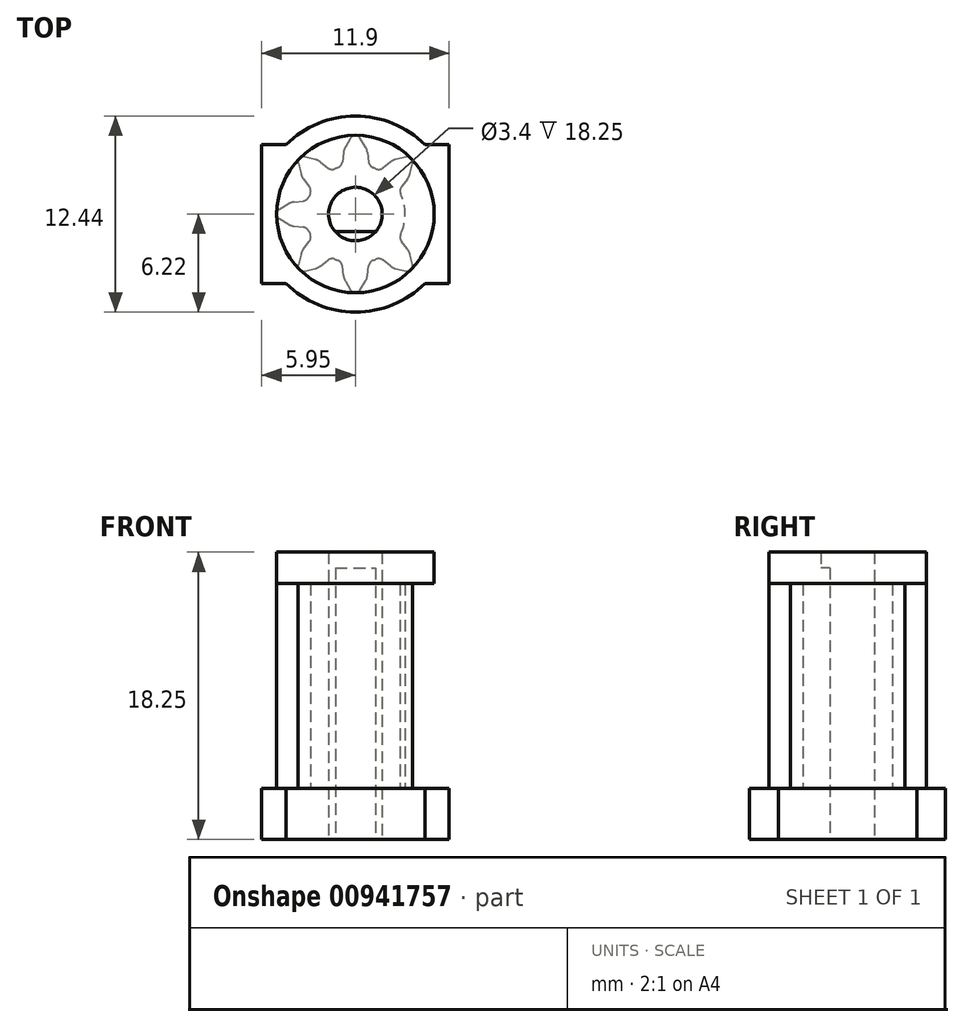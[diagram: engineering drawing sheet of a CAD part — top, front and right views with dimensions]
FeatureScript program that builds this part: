
annotation { "Feature Type Name" : "Feature", "Feature Type Description" : "" }
export const myFeature = defineFeature(function(context is Context, id is Id, definition is map)
    precondition{}
    {
        {
            var Q0;
            Q0=qCreatedBy(makeId("Top.planeOp"),FACE);
            var sketch = newSketch(context, id + "F0", { "sketchPlane" : qUnion([Q0])});
            skCircle(sketch, "E0", {"center": v(0, 0) * mm, "radius": 1.7 * mm});
            skCircle(sketch, "E1", {"center": v(0, 0) * mm, "radius": 2.55 * mm});
            skArc(sketch, "E2", {"start": v(-4.4, -4.4) * mm, "mid": v(0, -6.22) * mm, "end": v(4.4, -4.4) * mm});
            skCircle(sketch, "E3", {"center": v(0, 0) * mm, "radius": 3.15 * mm});
            skCircle(sketch, "E4", {"center": v(0, 0) * mm, "radius": 5 * mm});
            skLineSegment(sketch, "E5.bottom", {"start": v(-5.95, 4.4) * mm, "end": v(-4.4, 4.4) * mm});
            skLineSegment(sketch, "E5.top", {"start": v(-5.95, -4.4) * mm, "end": v(-4.4, -4.4) * mm});
            skLineSegment(sketch, "E5.left", {"start": v(-5.95, 4.4) * mm, "end": v(-5.95, -4.4) * mm});
            skLineSegment(sketch, "E5.right", {"start": v(5.95, 4.4) * mm, "end": v(5.95, -4.4) * mm});
            skArc(sketch, "E6.trimOffspring", {"start": v(4.4, 4.4) * mm, "mid": v(0, 6.22) * mm, "end": v(-4.4, 4.4) * mm});
            skLineSegment(sketch, "E7.trimOffspring", {"start": v(4.4, 4.4) * mm, "end": v(5.95, 4.4) * mm});
            skLineSegment(sketch, "E8.trimOffspring", {"start": v(4.4, -4.4) * mm, "end": v(5.95, -4.4) * mm});
            skLineSegment(sketch, "E9", {"start": v(0, 6.22) * mm, "end": v(0, -6.22) * mm, "construction": true});
            skLineSegment(sketch, "E10", {"start": v(-1.27, -1.12) * mm, "end": v(1.27, -1.12) * mm});
            skSolve(sketch);
        }
        {
            var Q0;
            Q0=makeQuery(id+"F0.imprint","IMPRINT",FACE,{"disambiguationData":[TD([[makeQuery(id+"F0.imprint","IMPRINT",EDGE,{"derivedFrom":sQuery(id+"F0.wireOp",EDGE,"E2")}),1.0]])]});
            var Q1;
            Q1=makeQuery(id+"F0.imprint","IMPRINT",FACE,{"disambiguationData":[TD([[makeQuery(id+"F0.imprint","IMPRINT",EDGE,{"derivedFrom":sQuery(id+"F0.wireOp",EDGE,"E3")}),-1.0]])]});
            var Q2;
            Q2=makeQuery(id+"F0.imprint","IMPRINT",FACE,{"disambiguationData":[TD([[makeQuery(id+"F0.imprint","IMPRINT",EDGE,{"derivedFrom":sQuery(id+"F0.wireOp",EDGE,"E0")}),-1.0]])]});
            var Q3;
            Q3=makeQuery(id+"F0.imprint","IMPRINT",FACE,{"disambiguationData":[TD([[makeQuery(id+"F0.imprint","IMPRINT",EDGE,{"derivedFrom":sQuery(id+"F0.wireOp",EDGE,"E1")}),-1.0]])]});
            var Q4;
            {var subQ0=sQuery(id+"F0.wireOp",EDGE,"Gm9W4LpN-Av9A-MbCA-gdo4-SThQoX5Y8GiM");Q4=makeQuery(id+"F0.imprint","IMPRINT",FACE,{"disambiguationData":[TD([[makeQuery(id+"F0.imprint","IMPRINT",EDGE,{"derivedFrom":subQ0}),-1.0]])]});}
            var Q5;
            {var subQ0=sQuery(id+"F0.wireOp",EDGE,"E10");Q5=makeQuery(id+"F0.imprint","IMPRINT",FACE,{"disambiguationData":[TD([[makeQuery(id+"F0.imprint","IMPRINT",EDGE,{"derivedFrom":subQ0}),-1.0]])]});}
            extrude(context, id + "F1", {"entities" : qUnion([Q0, Q1, Q2, Q3, Q4, Q5]), "depth" : 3.25 * mm, "offsetDistance" : 25 * mm});
        }
        {
            var Q0;
            Q0=makeQuery(id+"F1.opExtrude","CAP_FACE",FACE,{"disambiguationData":[OSD([sQuery(id+"F0.wireOp",EDGE,"E0"),sQuery(id+"F0.wireOp",EDGE,"E2"),sQuery(id+"F0.wireOp",EDGE,"E5.bottom"),sQuery(id+"F0.wireOp",EDGE,"E5.top"),sQuery(id+"F0.wireOp",EDGE,"E5.left"),sQuery(id+"F0.wireOp",EDGE,"E5.right"),sQuery(id+"F0.wireOp",EDGE,"E6.trimOffspring"),sQuery(id+"F0.wireOp",EDGE,"E7.trimOffspring"),sQuery(id+"F0.wireOp",EDGE,"E8.trimOffspring")])],"isStart":false});
            var sketch = newSketch(context, id + "F2", { "sketchPlane" : qUnion([Q0])});
            skCircle(sketch, "E11.0", {"center": v(0, 0) * mm, "radius": 5 * mm});
            skCircle(sketch, "E12.0", {"center": v(0, 0) * mm, "radius": 3.15 * mm});
            skCircle(sketch, "E13.0", {"center": v(0, 0) * mm, "radius": 2.55 * mm});
            skArc(sketch, "E14", {"start": v(4.83, -0.3) * mm, "mid": v(5, 0) * mm, "end": v(4.83, 0.3) * mm});
            skArc(sketch, "E15", {"start": v(3.31, -0.84) * mm, "mid": v(3.09, -0.93) * mm, "end": v(2.94, -1.13) * mm});
            skLineSegment(sketch, "E16", {"start": v(4.26, -0.64) * mm, "end": v(4.83, -0.3) * mm});
            skLineSegment(sketch, "E17", {"start": v(4.83, 0.3) * mm, "end": v(4.26, 0.64) * mm});
            skLineSegment(sketch, "E18", {"start": v(0, 0) * mm, "end": v(5.95, 0) * mm, "construction": true});
            skCircle(sketch, "E19.0", {"center": v(0, 0) * mm, "radius": 4.06 * mm, "construction": true});
            skArc(sketch, "E20", {"start": v(3.91, -0.76) * mm, "mid": v(4.1, -0.72) * mm, "end": v(4.26, -0.64) * mm});
            skLineSegment(sketch, "E21", {"start": v(3.91, -0.76) * mm, "end": v(3.31, -0.84) * mm});
            skArc(sketch, "E22.MirrorCS", {"start": v(3.91, 0.76) * mm, "mid": v(4.1, 0.72) * mm, "end": v(4.26, 0.64) * mm});
            skLineSegment(sketch, "E23.MirrorCS", {"start": v(3.91, 0.76) * mm, "end": v(3.31, 0.84) * mm});
            skArc(sketch, "E24.MirrorCS", {"start": v(3.31, 0.84) * mm, "mid": v(3.09, 0.93) * mm, "end": v(2.94, 1.13) * mm});
            skArc(sketch, "E25.1.0", {"start": v(1.75, -2.93) * mm, "mid": v(1.53, -2.84) * mm, "end": v(1.28, -2.88) * mm});
            skLineSegment(sketch, "E25.1.1", {"start": v(2.23, -3.3) * mm, "end": v(1.75, -2.93) * mm});
            skArc(sketch, "E25.1.2", {"start": v(2.23, -3.3) * mm, "mid": v(2.38, -3.4) * mm, "end": v(2.56, -3.47) * mm});
            skLineSegment(sketch, "E25.1.3", {"start": v(2.56, -3.47) * mm, "end": v(3.2, -3.63) * mm});
            skArc(sketch, "E25.1.4", {"start": v(3.2, -3.63) * mm, "mid": v(3.54, -3.54) * mm, "end": v(3.63, -3.2) * mm});
            skLineSegment(sketch, "E25.1.5", {"start": v(3.63, -3.2) * mm, "end": v(3.47, -2.56) * mm});
            skArc(sketch, "E25.1.6", {"start": v(3.3, -2.23) * mm, "mid": v(3.4, -2.38) * mm, "end": v(3.47, -2.56) * mm});
            skLineSegment(sketch, "E25.1.7", {"start": v(3.3, -2.23) * mm, "end": v(2.93, -1.75) * mm});
            skArc(sketch, "E25.1.8", {"start": v(2.93, -1.75) * mm, "mid": v(2.84, -1.53) * mm, "end": v(2.88, -1.28) * mm});
            skArc(sketch, "E25.2.0", {"start": v(-0.84, -3.31) * mm, "mid": v(-0.93, -3.09) * mm, "end": v(-1.12, -2.94) * mm});
            skLineSegment(sketch, "E25.2.1", {"start": v(-0.76, -3.91) * mm, "end": v(-0.84, -3.31) * mm});
            skArc(sketch, "E25.2.2", {"start": v(-0.76, -3.91) * mm, "mid": v(-0.72, -4.1) * mm, "end": v(-0.64, -4.26) * mm});
            skLineSegment(sketch, "E25.2.3", {"start": v(-0.64, -4.26) * mm, "end": v(-0.3, -4.83) * mm});
            skArc(sketch, "E25.2.4", {"start": v(-0.3, -4.83) * mm, "mid": v(0, -5) * mm, "end": v(0.3, -4.83) * mm});
            skLineSegment(sketch, "E25.2.5", {"start": v(0.3, -4.83) * mm, "end": v(0.64, -4.26) * mm});
            skArc(sketch, "E25.2.6", {"start": v(0.76, -3.91) * mm, "mid": v(0.72, -4.1) * mm, "end": v(0.64, -4.26) * mm});
            skLineSegment(sketch, "E25.2.7", {"start": v(0.76, -3.91) * mm, "end": v(0.84, -3.31) * mm});
            skArc(sketch, "E25.2.8", {"start": v(0.84, -3.31) * mm, "mid": v(0.93, -3.09) * mm, "end": v(1.13, -2.94) * mm});
            skArc(sketch, "E25.3.0", {"start": v(-2.93, -1.75) * mm, "mid": v(-2.84, -1.53) * mm, "end": v(-2.88, -1.28) * mm});
            skLineSegment(sketch, "E25.3.1", {"start": v(-3.3, -2.23) * mm, "end": v(-2.93, -1.75) * mm});
            skArc(sketch, "E25.3.2", {"start": v(-3.3, -2.23) * mm, "mid": v(-3.4, -2.38) * mm, "end": v(-3.47, -2.56) * mm});
            skLineSegment(sketch, "E25.3.3", {"start": v(-3.47, -2.56) * mm, "end": v(-3.63, -3.2) * mm});
            skArc(sketch, "E25.3.4", {"start": v(-3.63, -3.2) * mm, "mid": v(-3.54, -3.54) * mm, "end": v(-3.2, -3.63) * mm});
            skLineSegment(sketch, "E25.3.5", {"start": v(-3.2, -3.63) * mm, "end": v(-2.56, -3.47) * mm});
            skArc(sketch, "E25.3.6", {"start": v(-2.23, -3.3) * mm, "mid": v(-2.38, -3.4) * mm, "end": v(-2.56, -3.47) * mm});
            skLineSegment(sketch, "E25.3.7", {"start": v(-2.23, -3.3) * mm, "end": v(-1.75, -2.93) * mm});
            skArc(sketch, "E25.3.8", {"start": v(-1.75, -2.93) * mm, "mid": v(-1.53, -2.84) * mm, "end": v(-1.28, -2.88) * mm});
            skArc(sketch, "E25.4.0", {"start": v(-3.31, 0.84) * mm, "mid": v(-3.09, 0.93) * mm, "end": v(-2.94, 1.12) * mm});
            skLineSegment(sketch, "E25.4.1", {"start": v(-3.91, 0.76) * mm, "end": v(-3.31, 0.84) * mm});
            skArc(sketch, "E25.4.2", {"start": v(-3.91, 0.76) * mm, "mid": v(-4.1, 0.72) * mm, "end": v(-4.26, 0.64) * mm});
            skLineSegment(sketch, "E25.4.3", {"start": v(-4.26, 0.64) * mm, "end": v(-4.83, 0.3) * mm});
            skArc(sketch, "E25.4.4", {"start": v(-4.83, 0.3) * mm, "mid": v(-5, 0) * mm, "end": v(-4.83, -0.3) * mm});
            skLineSegment(sketch, "E25.4.5", {"start": v(-4.83, -0.3) * mm, "end": v(-4.26, -0.64) * mm});
            skArc(sketch, "E25.4.6", {"start": v(-3.91, -0.76) * mm, "mid": v(-4.1, -0.72) * mm, "end": v(-4.26, -0.64) * mm});
            skLineSegment(sketch, "E25.4.7", {"start": v(-3.91, -0.76) * mm, "end": v(-3.31, -0.84) * mm});
            skArc(sketch, "E25.4.8", {"start": v(-3.31, -0.84) * mm, "mid": v(-3.09, -0.93) * mm, "end": v(-2.94, -1.13) * mm});
            skArc(sketch, "E25.5.0", {"start": v(-1.75, 2.93) * mm, "mid": v(-1.53, 2.84) * mm, "end": v(-1.28, 2.88) * mm});
            skLineSegment(sketch, "E25.5.1", {"start": v(-2.23, 3.3) * mm, "end": v(-1.75, 2.93) * mm});
            skArc(sketch, "E25.5.2", {"start": v(-2.23, 3.3) * mm, "mid": v(-2.38, 3.4) * mm, "end": v(-2.56, 3.47) * mm});
            skLineSegment(sketch, "E25.5.3", {"start": v(-2.56, 3.47) * mm, "end": v(-3.2, 3.63) * mm});
            skArc(sketch, "E25.5.4", {"start": v(-3.2, 3.63) * mm, "mid": v(-3.54, 3.54) * mm, "end": v(-3.63, 3.2) * mm});
            skLineSegment(sketch, "E25.5.5", {"start": v(-3.63, 3.2) * mm, "end": v(-3.47, 2.56) * mm});
            skArc(sketch, "E25.5.6", {"start": v(-3.3, 2.23) * mm, "mid": v(-3.4, 2.38) * mm, "end": v(-3.47, 2.56) * mm});
            skLineSegment(sketch, "E25.5.7", {"start": v(-3.3, 2.23) * mm, "end": v(-2.93, 1.75) * mm});
            skArc(sketch, "E25.5.8", {"start": v(-2.93, 1.75) * mm, "mid": v(-2.84, 1.53) * mm, "end": v(-2.88, 1.28) * mm});
            skArc(sketch, "E25.6.0", {"start": v(0.84, 3.31) * mm, "mid": v(0.93, 3.09) * mm, "end": v(1.12, 2.94) * mm});
            skLineSegment(sketch, "E25.6.1", {"start": v(0.76, 3.91) * mm, "end": v(0.84, 3.31) * mm});
            skArc(sketch, "E25.6.2", {"start": v(0.76, 3.91) * mm, "mid": v(0.72, 4.1) * mm, "end": v(0.64, 4.26) * mm});
            skLineSegment(sketch, "E25.6.3", {"start": v(0.64, 4.26) * mm, "end": v(0.3, 4.83) * mm});
            skArc(sketch, "E25.6.4", {"start": v(0.3, 4.83) * mm, "mid": v(0, 5) * mm, "end": v(-0.3, 4.83) * mm});
            skLineSegment(sketch, "E25.6.5", {"start": v(-0.3, 4.83) * mm, "end": v(-0.64, 4.26) * mm});
            skArc(sketch, "E25.6.6", {"start": v(-0.76, 3.91) * mm, "mid": v(-0.72, 4.1) * mm, "end": v(-0.64, 4.26) * mm});
            skLineSegment(sketch, "E25.6.7", {"start": v(-0.76, 3.91) * mm, "end": v(-0.84, 3.31) * mm});
            skArc(sketch, "E25.6.8", {"start": v(-0.84, 3.31) * mm, "mid": v(-0.93, 3.09) * mm, "end": v(-1.13, 2.94) * mm});
            skArc(sketch, "E26.0.7.0", {"start": v(2.93, 1.75) * mm, "mid": v(2.84, 1.53) * mm, "end": v(2.88, 1.28) * mm});
            skLineSegment(sketch, "E26.4.7.0", {"start": v(3.3, 2.23) * mm, "end": v(2.93, 1.75) * mm});
            skArc(sketch, "E26.7.7.0", {"start": v(3.3, 2.23) * mm, "mid": v(3.4, 2.38) * mm, "end": v(3.47, 2.56) * mm});
            skLineSegment(sketch, "E26.11.7.0", {"start": v(3.47, 2.56) * mm, "end": v(3.63, 3.2) * mm});
            skArc(sketch, "E26.14.7.0", {"start": v(3.63, 3.2) * mm, "mid": v(3.54, 3.54) * mm, "end": v(3.2, 3.63) * mm});
            skLineSegment(sketch, "E26.18.7.0", {"start": v(3.2, 3.63) * mm, "end": v(2.56, 3.47) * mm});
            skArc(sketch, "E26.21.7.0", {"start": v(2.23, 3.3) * mm, "mid": v(2.38, 3.4) * mm, "end": v(2.56, 3.47) * mm});
            skLineSegment(sketch, "E26.25.7.0", {"start": v(2.23, 3.3) * mm, "end": v(1.75, 2.93) * mm});
            skArc(sketch, "E26.28.7.0", {"start": v(1.75, 2.93) * mm, "mid": v(1.53, 2.84) * mm, "end": v(1.28, 2.88) * mm});
            skArc(sketch, "E26.0.8.0", {"start": v(3.31, -0.84) * mm, "mid": v(3.09, -0.93) * mm, "end": v(2.94, -1.12) * mm});
            skSolve(sketch);
        }
        {
            var Q0;
            {var subQ1=sQuery(id+"F2.wireOp",EDGE,"E25.4.0");Q0=makeQuery(id+"F2.imprint","IMPRINT",FACE,{"disambiguationData":[TD([[makeQuery(id+"F2.imprint","IMPRINT",EDGE,{"derivedFrom":subQ1}),-1.0]])]});}
            var Q1;
            {var subQ4=sQuery(id+"F2.wireOp",EDGE,"E25.5.0");Q1=makeQuery(id+"F2.imprint","IMPRINT",FACE,{"disambiguationData":[TD([[makeQuery(id+"F2.imprint","IMPRINT",EDGE,{"derivedFrom":subQ4}),-1.0]])]});}
            var Q2;
            {var subQ3=sQuery(id+"F2.wireOp",EDGE,"E25.6.0");Q2=makeQuery(id+"F2.imprint","IMPRINT",FACE,{"disambiguationData":[TD([[makeQuery(id+"F2.imprint","IMPRINT",EDGE,{"derivedFrom":subQ3}),-1.0]])]});}
            var Q3;
            {var subQ0=sQuery(id+"F2.wireOp",EDGE,"E25.7.0");Q3=makeQuery(id+"F2.imprint","IMPRINT",FACE,{"disambiguationData":[TD([[makeQuery(id+"F2.imprint","IMPRINT",EDGE,{"derivedFrom":subQ0}),-1.0]])]});}
            var Q4;
            {var subQ4=sQuery(id+"F2.wireOp",EDGE,"E25.1.0");Q4=makeQuery(id+"F2.imprint","IMPRINT",FACE,{"disambiguationData":[TD([[makeQuery(id+"F2.imprint","IMPRINT",EDGE,{"derivedFrom":subQ4}),-1.0]])]});}
            var Q5;
            {var subQ0=sQuery(id+"F2.wireOp",EDGE,"E25.2.0");Q5=makeQuery(id+"F2.imprint","IMPRINT",FACE,{"disambiguationData":[TD([[makeQuery(id+"F2.imprint","IMPRINT",EDGE,{"derivedFrom":subQ0}),-1.0]])]});}
            var Q6;
            {var subQ4=sQuery(id+"F2.wireOp",EDGE,"E25.3.0");Q6=makeQuery(id+"F2.imprint","IMPRINT",FACE,{"disambiguationData":[TD([[makeQuery(id+"F2.imprint","IMPRINT",EDGE,{"derivedFrom":subQ4}),-1.0]])]});}
            var Q7;
            Q7=makeQuery(id+"F2.imprint","IMPRINT",FACE,{"disambiguationData":[TD([[makeQuery(id+"F2.imprint","IMPRINT",EDGE,{"derivedFrom":sQuery(id+"F2.wireOp",EDGE,"E13.0")}),-1.0]])]});
            var Q8;
            Q8=makeQuery(id+"F2.imprint","IMPRINT",FACE,{"disambiguationData":[TD([[makeQuery(id+"F2.imprint","IMPRINT",EDGE,{"derivedFrom":sQuery(id+"F2.wireOp",EDGE,"E13.0")}),1.0]])]});
            var Q9;
            {var subQ4=sQuery(id+"F2.wireOp",EDGE,"E26.0.7.0");Q9=makeQuery(id+"F2.imprint","IMPRINT",FACE,{"disambiguationData":[TD([[makeQuery(id+"F2.imprint","IMPRINT",EDGE,{"derivedFrom":subQ4}),-1.0]])]});}
            var Q10;
            {var subQ4=sQuery(id+"F2.wireOp",EDGE,"E26.0.8.0");Q10=makeQuery(id+"F2.imprint","IMPRINT",FACE,{"disambiguationData":[TD([[makeQuery(id+"F2.imprint","IMPRINT",EDGE,{"derivedFrom":subQ4}),-1.0]])]});}
            extrude(context, id + "F3", {"entities" : qUnion([Q0, Q1, Q2, Q3, Q4, Q5, Q6, Q7, Q8, Q9, Q10]), "operationType" : NewBodyOperationType.ADD, "depth" : 14 * mm, "offsetDistance" : 25 * mm});
        }
        {
            var Q0;
            Q0=makeQuery(id+"F3.opExtrude","CAP_FACE",FACE,{"disambiguationData":[OSD([sQuery(id+"F0.wireOp",EDGE,"E0"),sQuery(id+"F0.wireOp",EDGE,"E10"),sQuery(id+"F2.wireOp",EDGE,"E12.0"),sQuery(id+"F2.wireOp",EDGE,"E25.1.0"),sQuery(id+"F2.wireOp",EDGE,"E25.1.1"),sQuery(id+"F2.wireOp",EDGE,"E25.1.2"),sQuery(id+"F2.wireOp",EDGE,"E25.1.3"),sQuery(id+"F2.wireOp",EDGE,"E25.1.4"),sQuery(id+"F2.wireOp",EDGE,"E25.1.5"),sQuery(id+"F2.wireOp",EDGE,"E25.1.6"),sQuery(id+"F2.wireOp",EDGE,"E25.1.7"),sQuery(id+"F2.wireOp",EDGE,"E25.1.8"),sQuery(id+"F2.wireOp",EDGE,"E25.2.0"),sQuery(id+"F2.wireOp",EDGE,"E25.2.1"),sQuery(id+"F2.wireOp",EDGE,"E25.2.2"),sQuery(id+"F2.wireOp",EDGE,"E25.2.3"),sQuery(id+"F2.wireOp",EDGE,"E25.2.4"),sQuery(id+"F2.wireOp",EDGE,"E25.2.5"),sQuery(id+"F2.wireOp",EDGE,"E25.2.6"),sQuery(id+"F2.wireOp",EDGE,"E25.2.7"),sQuery(id+"F2.wireOp",EDGE,"E25.2.8"),sQuery(id+"F2.wireOp",EDGE,"E25.3.0"),sQuery(id+"F2.wireOp",EDGE,"E25.3.1"),sQuery(id+"F2.wireOp",EDGE,"E25.3.2"),sQuery(id+"F2.wireOp",EDGE,"E25.3.3"),sQuery(id+"F2.wireOp",EDGE,"E25.3.4"),sQuery(id+"F2.wireOp",EDGE,"E25.3.5"),sQuery(id+"F2.wireOp",EDGE,"E25.3.6"),sQuery(id+"F2.wireOp",EDGE,"E25.3.7"),sQuery(id+"F2.wireOp",EDGE,"E25.3.8"),sQuery(id+"F2.wireOp",EDGE,"E25.4.0"),sQuery(id+"F2.wireOp",EDGE,"E25.4.1"),sQuery(id+"F2.wireOp",EDGE,"E25.4.2"),sQuery(id+"F2.wireOp",EDGE,"E25.4.3"),sQuery(id+"F2.wireOp",EDGE,"E25.4.4"),sQuery(id+"F2.wireOp",EDGE,"E25.4.5"),sQuery(id+"F2.wireOp",EDGE,"E25.4.6"),sQuery(id+"F2.wireOp",EDGE,"E25.4.7"),sQuery(id+"F2.wireOp",EDGE,"E25.4.8"),sQuery(id+"F2.wireOp",EDGE,"E25.5.0"),sQuery(id+"F2.wireOp",EDGE,"E25.5.1"),sQuery(id+"F2.wireOp",EDGE,"E25.5.2"),sQuery(id+"F2.wireOp",EDGE,"E25.5.3"),sQuery(id+"F2.wireOp",EDGE,"E25.5.4"),sQuery(id+"F2.wireOp",EDGE,"E25.5.5"),sQuery(id+"F2.wireOp",EDGE,"E25.5.6"),sQuery(id+"F2.wireOp",EDGE,"E25.5.7"),sQuery(id+"F2.wireOp",EDGE,"E25.5.8"),sQuery(id+"F2.wireOp",EDGE,"E25.6.0"),sQuery(id+"F2.wireOp",EDGE,"E25.6.1"),sQuery(id+"F2.wireOp",EDGE,"E25.6.2"),sQuery(id+"F2.wireOp",EDGE,"E25.6.3"),sQuery(id+"F2.wireOp",EDGE,"E25.6.4"),sQuery(id+"F2.wireOp",EDGE,"E25.6.5"),sQuery(id+"F2.wireOp",EDGE,"E25.6.6"),sQuery(id+"F2.wireOp",EDGE,"E25.6.7"),sQuery(id+"F2.wireOp",EDGE,"E25.6.8"),sQuery(id+"F2.wireOp",EDGE,"E26.0.7.0"),sQuery(id+"F2.wireOp",EDGE,"E26.4.7.0"),sQuery(id+"F2.wireOp",EDGE,"E26.7.7.0"),sQuery(id+"F2.wireOp",EDGE,"E26.11.7.0"),sQuery(id+"F2.wireOp",EDGE,"E26.14.7.0"),sQuery(id+"F2.wireOp",EDGE,"E26.18.7.0"),sQuery(id+"F2.wireOp",EDGE,"E26.21.7.0"),sQuery(id+"F2.wireOp",EDGE,"E26.25.7.0"),sQuery(id+"F2.wireOp",EDGE,"E26.28.7.0"),sQuery(id+"F2.wireOp",EDGE,"E26.0.8.0"),sQuery(id+"F2.wireOp",EDGE,"E21"),sQuery(id+"F2.wireOp",EDGE,"E20"),sQuery(id+"F2.wireOp",EDGE,"E16"),sQuery(id+"F2.wireOp",EDGE,"E14"),sQuery(id+"F2.wireOp",EDGE,"E17"),sQuery(id+"F2.wireOp",EDGE,"E22.MirrorCS"),sQuery(id+"F2.wireOp",EDGE,"E23.MirrorCS"),sQuery(id+"F2.wireOp",EDGE,"E24.MirrorCS")])],"isStart":false});
            var sketch = newSketch(context, id + "F4", { "sketchPlane" : qUnion([Q0])});
            skCircle(sketch, "E27", {"center": v(0, 0) * mm, "radius": 5 * mm});
            skCircle(sketch, "E28", {"center": v(0, 0) * mm, "radius": 1.7 * mm});
            skSolve(sketch);
        }
        {
            var Q0;
            {var subQ8=sQuery(id+"F2.wireOp",EDGE,"E25.5.0");Q0=makeQuery(id+"F4.imprint","IMPRINT",FACE,{"disambiguationData":[TD([[makeQuery(id+"F4.imprint","IMPRINT",EDGE,{"derivedFrom":makeQuery(id+"F3.opExtrude","CAP_EDGE",EDGE,{"disambiguationData":[OSD([subQ8])],"isStart":false})}),1.0]])]});}
            var Q1;
            {var subQ7=sQuery(id+"F2.wireOp",EDGE,"E25.4.0");Q1=makeQuery(id+"F4.imprint","IMPRINT",FACE,{"disambiguationData":[TD([[makeQuery(id+"F4.imprint","IMPRINT",EDGE,{"derivedFrom":makeQuery(id+"F3.opExtrude","CAP_EDGE",EDGE,{"disambiguationData":[OSD([subQ7])],"isStart":false})}),1.0]])]});}
            var Q2;
            {var subQ8=sQuery(id+"F2.wireOp",EDGE,"E25.6.0");Q2=makeQuery(id+"F4.imprint","IMPRINT",FACE,{"disambiguationData":[TD([[makeQuery(id+"F4.imprint","IMPRINT",EDGE,{"derivedFrom":makeQuery(id+"F3.opExtrude","CAP_EDGE",EDGE,{"disambiguationData":[OSD([subQ8])],"isStart":false})}),1.0]])]});}
            var Q3;
            {var subQ7=sQuery(id+"F2.wireOp",EDGE,"E26.0.7.0");Q3=makeQuery(id+"F4.imprint","IMPRINT",FACE,{"disambiguationData":[TD([[makeQuery(id+"F4.imprint","IMPRINT",EDGE,{"derivedFrom":makeQuery(id+"F3.opExtrude","CAP_EDGE",EDGE,{"disambiguationData":[OSD([subQ7])],"isStart":false})}),1.0]])]});}
            var Q4;
            {var subQ9=makeQuery(id+"F3.opExtrude","CAP_EDGE",EDGE,{"disambiguationData":[OSD([sQuery(id+"F2.wireOp",EDGE,"E25.1.5")])],"isStart":false});Q4=makeQuery(id+"F4.imprint","IMPRINT",FACE,{"disambiguationData":[TD([[makeQuery(id+"F4.imprint","IMPRINT",EDGE,{"derivedFrom":subQ9}),-1.0]])]});}
            var Q5;
            {var subQ7=sQuery(id+"F2.wireOp",EDGE,"E25.1.0");Q5=makeQuery(id+"F4.imprint","IMPRINT",FACE,{"disambiguationData":[TD([[makeQuery(id+"F4.imprint","IMPRINT",EDGE,{"derivedFrom":makeQuery(id+"F3.opExtrude","CAP_EDGE",EDGE,{"disambiguationData":[OSD([subQ7])],"isStart":false})}),1.0]])]});}
            var Q6;
            {var subQ7=sQuery(id+"F2.wireOp",EDGE,"E25.2.0");Q6=makeQuery(id+"F4.imprint","IMPRINT",FACE,{"disambiguationData":[TD([[makeQuery(id+"F4.imprint","IMPRINT",EDGE,{"derivedFrom":makeQuery(id+"F3.opExtrude","CAP_EDGE",EDGE,{"disambiguationData":[OSD([subQ7])],"isStart":false})}),1.0]])]});}
            var Q7;
            {var subQ2=sQuery(id+"F2.wireOp",EDGE,"E25.3.0");Q7=makeQuery(id+"F4.imprint","IMPRINT",FACE,{"disambiguationData":[TD([[makeQuery(id+"F4.imprint","IMPRINT",EDGE,{"derivedFrom":makeQuery(id+"F3.opExtrude","CAP_EDGE",EDGE,{"disambiguationData":[OSD([subQ2])],"isStart":false})}),1.0]])]});}
            var Q8;
            {var subQ15=sQuery(id+"F2.wireOp",EDGE,"E25.1.0");Q8=makeQuery(id+"F4.imprint","IMPRINT",FACE,{"disambiguationData":[TD([[makeQuery(id+"F4.imprint","IMPRINT",EDGE,{"derivedFrom":makeQuery(id+"F3.opExtrude","CAP_EDGE",EDGE,{"disambiguationData":[OSD([subQ15])],"isStart":false})}),-1.0]])]});}
            extrude(context, id + "F5", {"entities" : qUnion([Q0, Q1, Q2, Q3, Q4, Q5, Q6, Q7, Q8]), "operationType" : NewBodyOperationType.ADD, "endBound" : BoundingType.SYMMETRIC, "depth" : 2 * mm, "offsetDistance" : 25 * mm});
        }
    });
